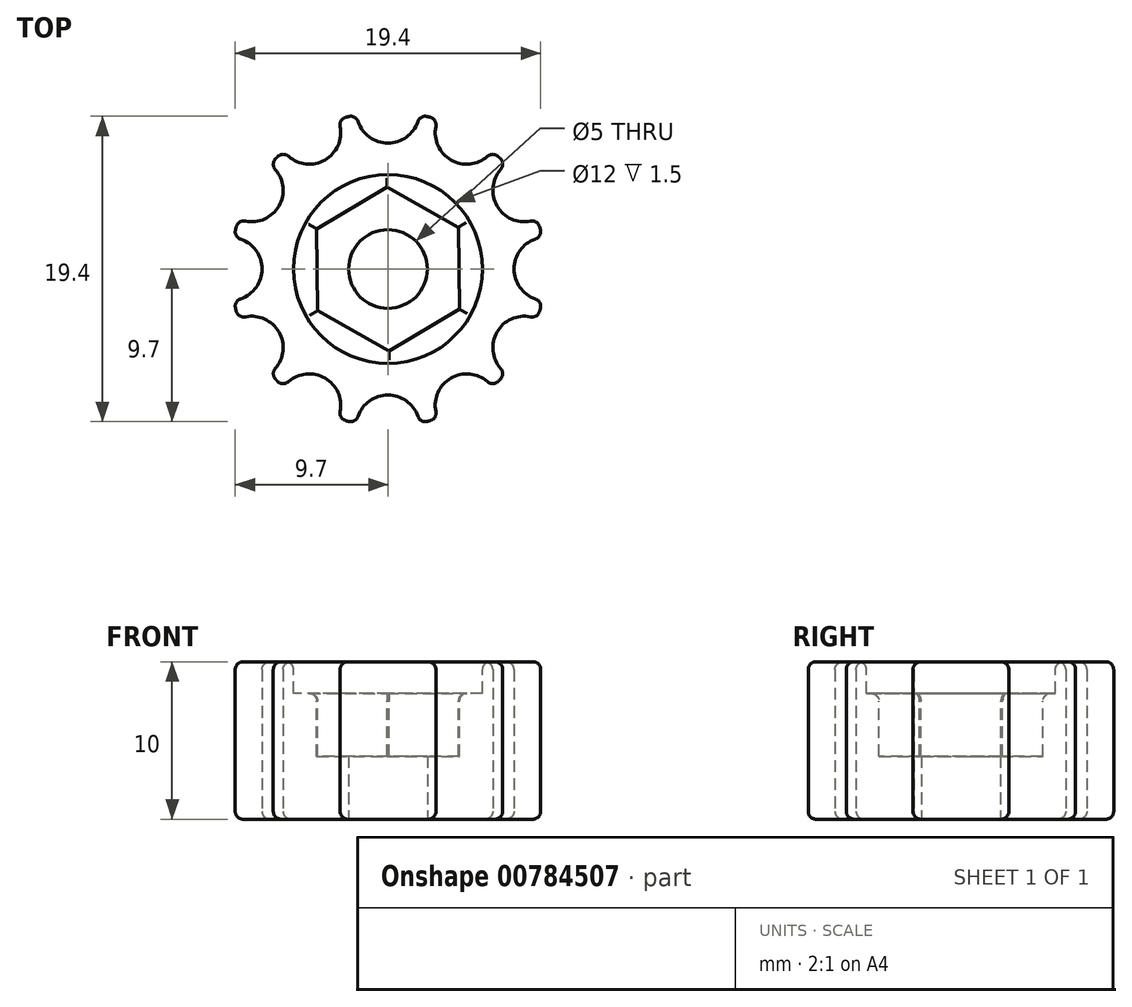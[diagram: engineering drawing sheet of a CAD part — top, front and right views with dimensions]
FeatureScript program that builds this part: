
annotation { "Feature Type Name" : "Feature", "Feature Type Description" : "" }
export const myFeature = defineFeature(function(context is Context, id is Id, definition is map)
    precondition{}
    {
        {
            var Q0;
            Q0=qCreatedBy(makeId("Top.planeOp"),FACE);
            var sketch = newSketch(context, id + "F0", { "sketchPlane" : qUnion([Q0])});
            skCircle(sketch, "E0", {"center": v(0, 0) * mm, "radius": 10 * mm});
            skCircle(sketch, "E1", {"center": v(0, 0) * mm, "radius": 8 * mm});
            skCircle(sketch, "E2", {"center": v(0, 10) * mm, "radius": 2 * mm});
            skCircle(sketch, "E3.1.0", {"center": v(-5, 8.66) * mm, "radius": 2 * mm});
            skCircle(sketch, "E3.2.0", {"center": v(-8.66, 5) * mm, "radius": 2 * mm});
            skCircle(sketch, "E3.3.0", {"center": v(-10, 0) * mm, "radius": 2 * mm});
            skCircle(sketch, "E3.4.0", {"center": v(-8.66, -5) * mm, "radius": 2 * mm});
            skCircle(sketch, "E3.5.0", {"center": v(-5, -8.66) * mm, "radius": 2 * mm});
            skCircle(sketch, "E3.6.0", {"center": v(0, -10) * mm, "radius": 2 * mm});
            skCircle(sketch, "E3.7.0", {"center": v(5, -8.66) * mm, "radius": 2 * mm});
            skCircle(sketch, "E3.8.0", {"center": v(8.66, -5) * mm, "radius": 2 * mm});
            skCircle(sketch, "E3.9.0", {"center": v(10, 0) * mm, "radius": 2 * mm});
            skCircle(sketch, "E3.10.0", {"center": v(8.66, 5) * mm, "radius": 2 * mm});
            skCircle(sketch, "E3.11.0", {"center": v(5, 8.66) * mm, "radius": 2 * mm});
            skCircle(sketch, "E4", {"center": v(0, 0) * mm, "radius": 2.5 * mm});
            skSolve(sketch);
        }
        {
            var Q0;
            {var subQ0=sQuery(id+"F0.wireOp",EDGE,"E1");var subQ8=makeQuery(id+"F0.imprint","INTERSECT",VERTEX,{"derivedFrom":[subQ0,sQuery(id+"F0.wireOp",EDGE,"E3.10.0")]});Q0=makeQuery(id+"F0.imprint","IMPRINT",FACE,{"disambiguationData":[TD([[makeQuery(id+"F0.imprint","IMPRINT",EDGE,{"disambiguationData":[TD([[subQ8,1.0]])],"derivedFrom":subQ0}),1.0]])]});}
            var Q1;
            {var subQ0=sQuery(id+"F0.wireOp",EDGE,"E3.1.0");var subQ1=sQuery(id+"F0.wireOp",EDGE,"E0");var subQ2=makeQuery(id+"F0.imprint","INTERSECT",VERTEX,{"disambiguationData":[OD(1.0)],"derivedFrom":[subQ1,subQ0]});Q1=makeQuery(id+"F0.imprint","IMPRINT",FACE,{"disambiguationData":[TD([[makeQuery(id+"F0.imprint","IMPRINT",EDGE,{"disambiguationData":[TD([[subQ2,-1.0]])],"derivedFrom":subQ1}),1.0]])]});}
            var Q2;
            {var subQ0=sQuery(id+"F0.wireOp",EDGE,"E2");var subQ1=sQuery(id+"F0.wireOp",EDGE,"E0");var subQ2=makeQuery(id+"F0.imprint","INTERSECT",VERTEX,{"disambiguationData":[OD(1.0)],"derivedFrom":[subQ1,subQ0]});Q2=makeQuery(id+"F0.imprint","IMPRINT",FACE,{"disambiguationData":[TD([[makeQuery(id+"F0.imprint","IMPRINT",EDGE,{"disambiguationData":[TD([[subQ2,-1.0]])],"derivedFrom":subQ1}),1.0]])]});}
            var Q3;
            {var subQ0=sQuery(id+"F0.wireOp",EDGE,"E3.11.0");var subQ1=sQuery(id+"F0.wireOp",EDGE,"E0");var subQ2=makeQuery(id+"F0.imprint","INTERSECT",VERTEX,{"disambiguationData":[OD(1.0)],"derivedFrom":[subQ1,subQ0]});Q3=makeQuery(id+"F0.imprint","IMPRINT",FACE,{"disambiguationData":[TD([[makeQuery(id+"F0.imprint","IMPRINT",EDGE,{"disambiguationData":[TD([[subQ2,-1.0]])],"derivedFrom":subQ1}),1.0]])]});}
            var Q4;
            {var subQ0=sQuery(id+"F0.wireOp",EDGE,"E3.10.0");var subQ1=sQuery(id+"F0.wireOp",EDGE,"E0");var subQ2=makeQuery(id+"F0.imprint","INTERSECT",VERTEX,{"disambiguationData":[OD(1.0)],"derivedFrom":[subQ1,subQ0]});Q4=makeQuery(id+"F0.imprint","IMPRINT",FACE,{"disambiguationData":[TD([[makeQuery(id+"F0.imprint","IMPRINT",EDGE,{"disambiguationData":[TD([[subQ2,-1.0]])],"derivedFrom":subQ1}),1.0]])]});}
            var Q5;
            {var subQ0=sQuery(id+"F0.wireOp",EDGE,"E3.10.0");var subQ1=sQuery(id+"F0.wireOp",EDGE,"E0");var subQ2=makeQuery(id+"F0.imprint","INTERSECT",VERTEX,{"disambiguationData":[OD(0.0)],"derivedFrom":[subQ1,subQ0]});Q5=makeQuery(id+"F0.imprint","IMPRINT",FACE,{"disambiguationData":[TD([[makeQuery(id+"F0.imprint","IMPRINT",EDGE,{"disambiguationData":[TD([[subQ2,1.0]])],"derivedFrom":subQ1}),1.0]])]});}
            var Q6;
            {var subQ0=sQuery(id+"F0.wireOp",EDGE,"E3.8.0");var subQ1=sQuery(id+"F0.wireOp",EDGE,"E0");var subQ2=makeQuery(id+"F0.imprint","INTERSECT",VERTEX,{"disambiguationData":[OD(1.0)],"derivedFrom":[subQ1,subQ0]});Q6=makeQuery(id+"F0.imprint","IMPRINT",FACE,{"disambiguationData":[TD([[makeQuery(id+"F0.imprint","IMPRINT",EDGE,{"disambiguationData":[TD([[subQ2,-1.0]])],"derivedFrom":subQ1}),1.0]])]});}
            var Q7;
            {var subQ0=sQuery(id+"F0.wireOp",EDGE,"E3.7.0");var subQ1=sQuery(id+"F0.wireOp",EDGE,"E0");var subQ2=makeQuery(id+"F0.imprint","INTERSECT",VERTEX,{"disambiguationData":[OD(1.0)],"derivedFrom":[subQ1,subQ0]});Q7=makeQuery(id+"F0.imprint","IMPRINT",FACE,{"disambiguationData":[TD([[makeQuery(id+"F0.imprint","IMPRINT",EDGE,{"disambiguationData":[TD([[subQ2,-1.0]])],"derivedFrom":subQ1}),1.0]])]});}
            var Q8;
            {var subQ0=sQuery(id+"F0.wireOp",EDGE,"E3.6.0");var subQ1=sQuery(id+"F0.wireOp",EDGE,"E0");var subQ2=makeQuery(id+"F0.imprint","INTERSECT",VERTEX,{"disambiguationData":[OD(1.0)],"derivedFrom":[subQ1,subQ0]});Q8=makeQuery(id+"F0.imprint","IMPRINT",FACE,{"disambiguationData":[TD([[makeQuery(id+"F0.imprint","IMPRINT",EDGE,{"disambiguationData":[TD([[subQ2,-1.0]])],"derivedFrom":subQ1}),1.0]])]});}
            var Q9;
            {var subQ0=sQuery(id+"F0.wireOp",EDGE,"E3.5.0");var subQ1=sQuery(id+"F0.wireOp",EDGE,"E0");var subQ2=makeQuery(id+"F0.imprint","INTERSECT",VERTEX,{"disambiguationData":[OD(1.0)],"derivedFrom":[subQ1,subQ0]});Q9=makeQuery(id+"F0.imprint","IMPRINT",FACE,{"disambiguationData":[TD([[makeQuery(id+"F0.imprint","IMPRINT",EDGE,{"disambiguationData":[TD([[subQ2,-1.0]])],"derivedFrom":subQ1}),1.0]])]});}
            var Q10;
            {var subQ0=sQuery(id+"F0.wireOp",EDGE,"E3.4.0");var subQ1=sQuery(id+"F0.wireOp",EDGE,"E0");var subQ2=makeQuery(id+"F0.imprint","INTERSECT",VERTEX,{"disambiguationData":[OD(1.0)],"derivedFrom":[subQ1,subQ0]});Q10=makeQuery(id+"F0.imprint","IMPRINT",FACE,{"disambiguationData":[TD([[makeQuery(id+"F0.imprint","IMPRINT",EDGE,{"disambiguationData":[TD([[subQ2,-1.0]])],"derivedFrom":subQ1}),1.0]])]});}
            var Q11;
            {var subQ0=sQuery(id+"F0.wireOp",EDGE,"E3.3.0");var subQ1=sQuery(id+"F0.wireOp",EDGE,"E0");var subQ2=makeQuery(id+"F0.imprint","INTERSECT",VERTEX,{"disambiguationData":[OD(1.0)],"derivedFrom":[subQ1,subQ0]});Q11=makeQuery(id+"F0.imprint","IMPRINT",FACE,{"disambiguationData":[TD([[makeQuery(id+"F0.imprint","IMPRINT",EDGE,{"disambiguationData":[TD([[subQ2,-1.0]])],"derivedFrom":subQ1}),1.0]])]});}
            var Q12;
            {var subQ0=sQuery(id+"F0.wireOp",EDGE,"E3.2.0");var subQ1=sQuery(id+"F0.wireOp",EDGE,"E0");var subQ2=makeQuery(id+"F0.imprint","INTERSECT",VERTEX,{"disambiguationData":[OD(1.0)],"derivedFrom":[subQ1,subQ0]});Q12=makeQuery(id+"F0.imprint","IMPRINT",FACE,{"disambiguationData":[TD([[makeQuery(id+"F0.imprint","IMPRINT",EDGE,{"disambiguationData":[TD([[subQ2,-1.0]])],"derivedFrom":subQ1}),1.0]])]});}
            extrude(context, id + "F1", {"entities" : qUnion([Q0, Q1, Q2, Q3, Q4, Q5, Q6, Q7, Q8, Q9, Q10, Q11, Q12]), "depth" : 10 * mm, "offsetDistance" : 25 * mm});
        }
        {
            var Q0;
            Q0=makeQuery(id+"F0.imprint","IMPRINT",FACE,{"disambiguationData":[TD([[makeQuery(id+"F0.imprint","IMPRINT",EDGE,{"derivedFrom":sQuery(id+"F0.wireOp",EDGE,"E4")}),1.0]])]});
            extrude(context, id + "F2", {"entities" : qUnion([Q0]), "operationType" : NewBodyOperationType.REMOVE, "depth" : 25 * mm, "offsetDistance" : 25 * mm});
        }
        {
            var Q0;
            Q0=makeQuery(id+"F1.opExtrude","CAP_FACE",FACE,{"disambiguationData":[OSD([sQuery(id+"F0.wireOp",EDGE,"E0"),sQuery(id+"F0.wireOp",EDGE,"E2"),sQuery(id+"F0.wireOp",EDGE,"E3.1.0"),sQuery(id+"F0.wireOp",EDGE,"E3.2.0"),sQuery(id+"F0.wireOp",EDGE,"E3.3.0"),sQuery(id+"F0.wireOp",EDGE,"E3.4.0"),sQuery(id+"F0.wireOp",EDGE,"E3.5.0"),sQuery(id+"F0.wireOp",EDGE,"E3.6.0"),sQuery(id+"F0.wireOp",EDGE,"E3.7.0"),sQuery(id+"F0.wireOp",EDGE,"E3.8.0"),sQuery(id+"F0.wireOp",EDGE,"E3.9.0"),sQuery(id+"F0.wireOp",EDGE,"E3.10.0"),sQuery(id+"F0.wireOp",EDGE,"E3.11.0"),sQuery(id+"F0.wireOp",EDGE,"E4")])],"isStart":false});
            var sketch = newSketch(context, id + "F3", { "sketchPlane" : qUnion([Q0])});
            skCircle(sketch, "E5", {"center": v(0, 0) * mm, "radius": 6 * mm});
            skCircle(sketch, "E6.cCircle", {"center": v(0, 0) * mm, "radius": 4.5 * mm, "construction": true});
            skLineSegment(sketch, "E6.0", {"start": v(4.53, -2.55) * mm, "end": v(0.06, -5.2) * mm});
            skLineSegment(sketch, "E6.1", {"start": v(0.06, -5.2) * mm, "end": v(-4.47, -2.65) * mm});
            skLineSegment(sketch, "E6.2", {"start": v(-4.47, -2.65) * mm, "end": v(-4.53, 2.55) * mm});
            skLineSegment(sketch, "E6.3", {"start": v(-4.53, 2.55) * mm, "end": v(-0.06, 5.2) * mm});
            skLineSegment(sketch, "E6.4", {"start": v(-0.06, 5.2) * mm, "end": v(4.47, 2.65) * mm});
            skLineSegment(sketch, "E6.5", {"start": v(4.47, 2.65) * mm, "end": v(4.53, -2.55) * mm});
            skPoint(sketch, "E6.0.midPoint", {"position": v(2.3, -3.87) * mm});
            skSolve(sketch);
        }
        {
            var Q0;
            Q0=makeQuery(id+"F3.imprint","IMPRINT",FACE,{"disambiguationData":[TD([[makeQuery(id+"F3.imprint","IMPRINT",EDGE,{"derivedFrom":sQuery(id+"F3.wireOp",EDGE,"E5")}),1.0]])]});
            var Q1;
            Q1=makeQuery(id+"F3.imprint","IMPRINT",FACE,{"disambiguationData":[TD([[makeQuery(id+"F3.imprint","IMPRINT",EDGE,{"derivedFrom":sQuery(id+"F3.wireOp",EDGE,"E6.0")}),-1.0]])]});
            extrude(context, id + "F4", {"entities" : qUnion([Q0, Q1]), "operationType" : NewBodyOperationType.REMOVE, "oppositeDirection" : true, "depth" : 2 * mm, "offsetDistance" : 25 * mm});
        }
        {
            var Q0;
            Q0=makeQuery(id+"F3.imprint","IMPRINT",FACE,{"disambiguationData":[TD([[makeQuery(id+"F3.imprint","IMPRINT",EDGE,{"derivedFrom":sQuery(id+"F3.wireOp",EDGE,"E6.0")}),-1.0]])]});
            extrude(context, id + "F5", {"entities" : qUnion([Q0]), "operationType" : NewBodyOperationType.REMOVE, "oppositeDirection" : true, "depth" : 6 * mm, "offsetDistance" : 25 * mm});
        }
        {
            var Q0;
            {var subQ0=sQuery(id+"F0.wireOp",EDGE,"E0");Q0=makeQuery(id+"F1.opExtrude","SWEPT_FACE",FACE,{"disambiguationData":[OSD([subQ0]),TDD([makeQuery(id+"F0.imprint","IMPRINT",EDGE,{"disambiguationData":[TD([[makeQuery(id+"F0.imprint","INTERSECT",VERTEX,{"disambiguationData":[OD(1.0)],"derivedFrom":[subQ0,sQuery(id+"F0.wireOp",EDGE,"E3.4.0")]}),-1.0]])],"derivedFrom":subQ0})])]});}
            var Q1;
            {var subQ0=sQuery(id+"F0.wireOp",EDGE,"E0");Q1=makeQuery(id+"F1.opExtrude","SWEPT_FACE",FACE,{"disambiguationData":[OSD([subQ0]),TDD([makeQuery(id+"F0.imprint","IMPRINT",EDGE,{"disambiguationData":[TD([[makeQuery(id+"F0.imprint","INTERSECT",VERTEX,{"disambiguationData":[OD(1.0)],"derivedFrom":[subQ0,sQuery(id+"F0.wireOp",EDGE,"E3.5.0")]}),-1.0]])],"derivedFrom":subQ0})])]});}
            var Q2;
            {var subQ0=sQuery(id+"F0.wireOp",EDGE,"E0");Q2=makeQuery(id+"F1.opExtrude","SWEPT_FACE",FACE,{"disambiguationData":[OSD([subQ0]),TDD([makeQuery(id+"F0.imprint","IMPRINT",EDGE,{"disambiguationData":[TD([[makeQuery(id+"F0.imprint","INTERSECT",VERTEX,{"disambiguationData":[OD(1.0)],"derivedFrom":[subQ0,sQuery(id+"F0.wireOp",EDGE,"E3.6.0")]}),-1.0]])],"derivedFrom":subQ0})])]});}
            var Q3;
            {var subQ0=sQuery(id+"F0.wireOp",EDGE,"E0");Q3=makeQuery(id+"F1.opExtrude","SWEPT_FACE",FACE,{"disambiguationData":[OSD([subQ0]),TDD([makeQuery(id+"F0.imprint","IMPRINT",EDGE,{"disambiguationData":[TD([[makeQuery(id+"F0.imprint","INTERSECT",VERTEX,{"disambiguationData":[OD(1.0)],"derivedFrom":[subQ0,sQuery(id+"F0.wireOp",EDGE,"E3.7.0")]}),-1.0]])],"derivedFrom":subQ0})])]});}
            var Q4;
            {var subQ0=sQuery(id+"F0.wireOp",EDGE,"E0");Q4=makeQuery(id+"F1.opExtrude","SWEPT_FACE",FACE,{"disambiguationData":[OSD([subQ0]),TDD([makeQuery(id+"F0.imprint","IMPRINT",EDGE,{"disambiguationData":[TD([[makeQuery(id+"F0.imprint","INTERSECT",VERTEX,{"disambiguationData":[OD(1.0)],"derivedFrom":[subQ0,sQuery(id+"F0.wireOp",EDGE,"E3.8.0")]}),-1.0]])],"derivedFrom":subQ0})])]});}
            var Q5;
            {var subQ0=sQuery(id+"F0.wireOp",EDGE,"E0");Q5=makeQuery(id+"F1.opExtrude","SWEPT_FACE",FACE,{"disambiguationData":[OSD([subQ0]),TDD([makeQuery(id+"F0.imprint","IMPRINT",EDGE,{"disambiguationData":[TD([[makeQuery(id+"F0.imprint","INTERSECT",VERTEX,{"disambiguationData":[OD(1.0)],"derivedFrom":[subQ0,sQuery(id+"F0.wireOp",EDGE,"E3.3.0")]}),-1.0]])],"derivedFrom":subQ0})])]});}
            var Q6;
            {var subQ0=sQuery(id+"F0.wireOp",EDGE,"E0");Q6=makeQuery(id+"F1.opExtrude","SWEPT_FACE",FACE,{"disambiguationData":[OSD([subQ0]),TDD([makeQuery(id+"F0.imprint","IMPRINT",EDGE,{"disambiguationData":[TD([[makeQuery(id+"F0.imprint","INTERSECT",VERTEX,{"disambiguationData":[OD(1.0)],"derivedFrom":[subQ0,sQuery(id+"F0.wireOp",EDGE,"E3.2.0")]}),-1.0]])],"derivedFrom":subQ0})])]});}
            var Q7;
            {var subQ0=sQuery(id+"F0.wireOp",EDGE,"E0");Q7=makeQuery(id+"F1.opExtrude","SWEPT_FACE",FACE,{"disambiguationData":[OSD([subQ0]),TDD([makeQuery(id+"F0.imprint","IMPRINT",EDGE,{"disambiguationData":[TD([[makeQuery(id+"F0.imprint","INTERSECT",VERTEX,{"disambiguationData":[OD(1.0)],"derivedFrom":[subQ0,sQuery(id+"F0.wireOp",EDGE,"E3.1.0")]}),-1.0]])],"derivedFrom":subQ0})])]});}
            var Q8;
            {var subQ0=sQuery(id+"F0.wireOp",EDGE,"E0");Q8=makeQuery(id+"F1.opExtrude","SWEPT_FACE",FACE,{"disambiguationData":[OSD([subQ0]),TDD([makeQuery(id+"F0.imprint","IMPRINT",EDGE,{"disambiguationData":[TD([[makeQuery(id+"F0.imprint","INTERSECT",VERTEX,{"disambiguationData":[OD(1.0)],"derivedFrom":[subQ0,sQuery(id+"F0.wireOp",EDGE,"E2")]}),-1.0]])],"derivedFrom":subQ0})])]});}
            var Q9;
            {var subQ0=sQuery(id+"F0.wireOp",EDGE,"E0");Q9=makeQuery(id+"F1.opExtrude","SWEPT_FACE",FACE,{"disambiguationData":[OSD([subQ0]),TDD([makeQuery(id+"F0.imprint","IMPRINT",EDGE,{"disambiguationData":[TD([[makeQuery(id+"F0.imprint","INTERSECT",VERTEX,{"disambiguationData":[OD(1.0)],"derivedFrom":[subQ0,sQuery(id+"F0.wireOp",EDGE,"E3.11.0")]}),-1.0]])],"derivedFrom":subQ0})])]});}
            var Q10;
            {var subQ0=sQuery(id+"F0.wireOp",EDGE,"E0");Q10=makeQuery(id+"F1.opExtrude","SWEPT_FACE",FACE,{"disambiguationData":[OSD([subQ0]),TDD([makeQuery(id+"F0.imprint","IMPRINT",EDGE,{"disambiguationData":[TD([[makeQuery(id+"F0.imprint","INTERSECT",VERTEX,{"disambiguationData":[OD(1.0)],"derivedFrom":[subQ0,sQuery(id+"F0.wireOp",EDGE,"E3.10.0")]}),-1.0]])],"derivedFrom":subQ0})])]});}
            var Q11;
            {var subQ0=sQuery(id+"F0.wireOp",EDGE,"E0");Q11=makeQuery(id+"F1.opExtrude","SWEPT_FACE",FACE,{"disambiguationData":[OSD([subQ0]),TDD([makeQuery(id+"F0.imprint","IMPRINT",EDGE,{"disambiguationData":[TD([[makeQuery(id+"F0.imprint","INTERSECT",VERTEX,{"disambiguationData":[OD(0.0)],"derivedFrom":[subQ0,sQuery(id+"F0.wireOp",EDGE,"E3.10.0")]}),1.0]])],"derivedFrom":subQ0})])]});}
            var Q12;
            Q12=makeQuery(id+"F1.opExtrude","CAP_FACE",FACE,{"disambiguationData":[OSD([sQuery(id+"F0.wireOp",EDGE,"E0"),sQuery(id+"F0.wireOp",EDGE,"E2"),sQuery(id+"F0.wireOp",EDGE,"E3.1.0"),sQuery(id+"F0.wireOp",EDGE,"E3.2.0"),sQuery(id+"F0.wireOp",EDGE,"E3.3.0"),sQuery(id+"F0.wireOp",EDGE,"E3.4.0"),sQuery(id+"F0.wireOp",EDGE,"E3.5.0"),sQuery(id+"F0.wireOp",EDGE,"E3.6.0"),sQuery(id+"F0.wireOp",EDGE,"E3.7.0"),sQuery(id+"F0.wireOp",EDGE,"E3.8.0"),sQuery(id+"F0.wireOp",EDGE,"E3.9.0"),sQuery(id+"F0.wireOp",EDGE,"E3.10.0"),sQuery(id+"F0.wireOp",EDGE,"E3.11.0"),sQuery(id+"F0.wireOp",EDGE,"E4")])],"isStart":false});
            var Q13;
            Q13=makeQuery(id+"F1.opExtrude","CAP_EDGE",EDGE,{"disambiguationData":[OSD([sQuery(id+"F0.wireOp",EDGE,"E3.1.0")])],"isStart":true});
            var Q14;
            Q14=makeQuery(id+"F1.opExtrude","CAP_EDGE",EDGE,{"disambiguationData":[OSD([sQuery(id+"F0.wireOp",EDGE,"E3.2.0")])],"isStart":true});
            var Q15;
            Q15=makeQuery(id+"F1.opExtrude","CAP_EDGE",EDGE,{"disambiguationData":[OSD([sQuery(id+"F0.wireOp",EDGE,"E3.3.0")])],"isStart":true});
            var Q16;
            Q16=makeQuery(id+"F1.opExtrude","CAP_EDGE",EDGE,{"disambiguationData":[OSD([sQuery(id+"F0.wireOp",EDGE,"E3.4.0")])],"isStart":true});
            var Q17;
            Q17=makeQuery(id+"F1.opExtrude","CAP_EDGE",EDGE,{"disambiguationData":[OSD([sQuery(id+"F0.wireOp",EDGE,"E3.5.0")])],"isStart":true});
            var Q18;
            Q18=makeQuery(id+"F1.opExtrude","CAP_EDGE",EDGE,{"disambiguationData":[OSD([sQuery(id+"F0.wireOp",EDGE,"E3.6.0")])],"isStart":true});
            var Q19;
            Q19=makeQuery(id+"F1.opExtrude","CAP_EDGE",EDGE,{"disambiguationData":[OSD([sQuery(id+"F0.wireOp",EDGE,"E3.7.0")])],"isStart":true});
            var Q20;
            Q20=makeQuery(id+"F1.opExtrude","CAP_EDGE",EDGE,{"disambiguationData":[OSD([sQuery(id+"F0.wireOp",EDGE,"E3.8.0")])],"isStart":true});
            var Q21;
            Q21=makeQuery(id+"F1.opExtrude","CAP_EDGE",EDGE,{"disambiguationData":[OSD([sQuery(id+"F0.wireOp",EDGE,"E3.9.0")])],"isStart":true});
            var Q22;
            Q22=makeQuery(id+"F1.opExtrude","CAP_EDGE",EDGE,{"disambiguationData":[OSD([sQuery(id+"F0.wireOp",EDGE,"E3.10.0")])],"isStart":true});
            var Q23;
            Q23=makeQuery(id+"F1.opExtrude","CAP_EDGE",EDGE,{"disambiguationData":[OSD([sQuery(id+"F0.wireOp",EDGE,"E3.11.0")])],"isStart":true});
            var Q24;
            Q24=makeQuery(id+"F1.opExtrude","CAP_EDGE",EDGE,{"disambiguationData":[OSD([sQuery(id+"F0.wireOp",EDGE,"E2")])],"isStart":true});
            fillet(context, id + "F6", {"entities" : qUnion([Q0, Q1, Q2, Q3, Q4, Q5, Q6, Q7, Q8, Q9, Q10, Q11, Q12, Q13, Q14, Q15, Q16, Q17, Q18, Q19, Q20, Q21, Q22, Q23, Q24]), "radius" : 0.5 * mm, "tangentPropagation" : true, "allowEdgeOverflow" : false});
        }
        {
            var Q0;
            Q0=makeQuery(id+"F5.boolean.opBoolean","INTERSECT",EDGE,{"derivedFrom":[makeQuery(id+"F4.boolean.opBoolean","COPY",FACE,{"derivedFrom":makeQuery(id+"F4.opExtrude","CAP_FACE",FACE,{"disambiguationData":[OSD([sQuery(id+"F0.wireOp",EDGE,"E4"),sQuery(id+"F3.wireOp",EDGE,"E5")])],"isStart":false})}),makeQuery(id+"F5.opExtrude","SWEPT_FACE",FACE,{"disambiguationData":[OSD([sQuery(id+"F3.wireOp",EDGE,"E6.4")])]})]});
            var Q1;
            Q1=makeQuery(id+"F5.boolean.opBoolean","INTERSECT",EDGE,{"derivedFrom":[makeQuery(id+"F4.boolean.opBoolean","COPY",FACE,{"derivedFrom":makeQuery(id+"F4.opExtrude","CAP_FACE",FACE,{"disambiguationData":[OSD([sQuery(id+"F0.wireOp",EDGE,"E4"),sQuery(id+"F3.wireOp",EDGE,"E5")])],"isStart":false})}),makeQuery(id+"F5.opExtrude","SWEPT_FACE",FACE,{"disambiguationData":[OSD([sQuery(id+"F3.wireOp",EDGE,"E6.5")])]})]});
            var Q2;
            Q2=makeQuery(id+"F5.boolean.opBoolean","INTERSECT",EDGE,{"derivedFrom":[makeQuery(id+"F4.boolean.opBoolean","COPY",FACE,{"derivedFrom":makeQuery(id+"F4.opExtrude","CAP_FACE",FACE,{"disambiguationData":[OSD([sQuery(id+"F0.wireOp",EDGE,"E4"),sQuery(id+"F3.wireOp",EDGE,"E5")])],"isStart":false})}),makeQuery(id+"F5.opExtrude","SWEPT_FACE",FACE,{"disambiguationData":[OSD([sQuery(id+"F3.wireOp",EDGE,"E6.0")])]})]});
            var Q3;
            Q3=makeQuery(id+"F5.boolean.opBoolean","INTERSECT",EDGE,{"derivedFrom":[makeQuery(id+"F4.boolean.opBoolean","COPY",FACE,{"derivedFrom":makeQuery(id+"F4.opExtrude","CAP_FACE",FACE,{"disambiguationData":[OSD([sQuery(id+"F0.wireOp",EDGE,"E4"),sQuery(id+"F3.wireOp",EDGE,"E5")])],"isStart":false})}),makeQuery(id+"F5.opExtrude","SWEPT_FACE",FACE,{"disambiguationData":[OSD([sQuery(id+"F3.wireOp",EDGE,"E6.1")])]})]});
            var Q4;
            Q4=makeQuery(id+"F5.boolean.opBoolean","INTERSECT",EDGE,{"derivedFrom":[makeQuery(id+"F4.boolean.opBoolean","COPY",FACE,{"derivedFrom":makeQuery(id+"F4.opExtrude","CAP_FACE",FACE,{"disambiguationData":[OSD([sQuery(id+"F0.wireOp",EDGE,"E4"),sQuery(id+"F3.wireOp",EDGE,"E5")])],"isStart":false})}),makeQuery(id+"F5.opExtrude","SWEPT_FACE",FACE,{"disambiguationData":[OSD([sQuery(id+"F3.wireOp",EDGE,"E6.3")])]})]});
            var Q5;
            Q5=makeQuery(id+"F5.boolean.opBoolean","INTERSECT",EDGE,{"derivedFrom":[makeQuery(id+"F4.boolean.opBoolean","COPY",FACE,{"derivedFrom":makeQuery(id+"F4.opExtrude","CAP_FACE",FACE,{"disambiguationData":[OSD([sQuery(id+"F0.wireOp",EDGE,"E4"),sQuery(id+"F3.wireOp",EDGE,"E5")])],"isStart":false})}),makeQuery(id+"F5.opExtrude","SWEPT_FACE",FACE,{"disambiguationData":[OSD([sQuery(id+"F3.wireOp",EDGE,"E6.2")])]})]});
            fillet(context, id + "F7", {"entities" : qUnion([Q0, Q1, Q2, Q3, Q4, Q5]), "radius" : 0.5 * mm, "tangentPropagation" : true, "allowEdgeOverflow" : false});
        }
    });
